# Revit family: Thorn AVENUE WALL
name_source: partatom
category: Lighting Fixtures
revit_build: Autodesk Revit 2016 (Build: 20150220_1215(x64)
units: mm (PartAtom-declared; Revit-internal decimal feet)

## family parameters
Cut with Voids When Loaded = No
Host = Face
Light Source = Yes
OmniClass Number = 23.80.70.14
OmniClass Title = Luminaries for External Lighting
Part Type = Normal
Room Calculation Point = No
Round Connector Dimension = Use Diameter
Shared = No

## types (1)
- AVENUE W300 LED
    Apparent Load = 15 VA
    Assembly Code = D5020200
    Color Filter = 16777215
    Default Elevation = 0 mm  [stored 0 ft]
    Description = LED luminaire
    Dimming Lamp Color Temperature Shift = <None>
    Height = 362 mm  [stored 1.18766 ft]
    Lamp = LED
    Length = 313 mm  [stored 1.0269 ft]
    Manufacturer = Thorn Lighting
    Model = 96258554
    Photometric Web File = 96258554_(STD).IES
    Reflector = Thorn_PMMA_Opaque
    Tilt Angle = 90.00°
    URL = www.thornlighting.com/96258554
    Voltage = 230 V
    Width = 176 mm  [stored 0.577428 ft]

note: [stored X ft] marks values corroborated as IEEE doubles in the binary element streams (Revit-internal decimal feet)

## geometry (parser evidence)
native form markers: Sweep x3
no freeform markers — native parametric forms only
